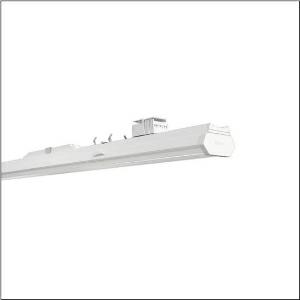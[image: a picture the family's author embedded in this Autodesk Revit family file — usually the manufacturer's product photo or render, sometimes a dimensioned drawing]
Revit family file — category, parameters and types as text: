
# Revit family: licross_r__11_protected_mo_51td12vn475f_93a6
name_source: partatom
category: Lighting Fixtures
units: mm (PartAtom-declared; Revit-internal decimal feet)

## family parameters
Cut with Voids When Loaded = No
Host = Face
Light Source = No
Part Type = Normal
Room Calculation Point = No
Round Connector Dimension = Use Diameter
Shared = No

## types (1)
- --- (1 x LED, 7910 lm, 49.3 W, 4000K)
    Apparent Load = 49 VA
    CIE Flux Codes = 73 92 98 99 100
    Color Rendering = 80
    Color Temperature = 4000K
    Default Elevation = 1800 mm
    Description = Licross® 11 Protected MO, luminaire insert, of sheet steel, galvanised, coil coated, white, length: 1.500mm, width: 90mm, height: 101mm, LED rated luminous flux: 7.910lm, light colour: 840, control gear: DALI 2, CLO, control gear: ECG DALI, with plug, 5-pole, with phase selection, mains connection: 220..240V, AC, 50/60Hz, halogen-free wiring, primary optical cover: cover, of PMMA, light emission: direct with ceiling illumination distribution, protection rating (complete): IP54, insulation class (complete): insulation class I (protective earthing), certification: CE, ENEC, VDE, UKCA, protection symbol: D if used in an environment with non-conductive dust loads with corresponding accessories, permissible ambient temperature for indoor applications: -25..+35°C, corresponds to IFS (International Featured Standards) requirements for safety and quality in the food industry, reducing of maximum allowable ambient temperature of 5°C with ceiling mounting, LABS conformity tested according to VDMA 24364:2018-05, packaging unit: 1 piece
    Height = 92 mm
    Lamp = 1 x LED
    Lamp Light Flux = 7910 lm
    Lamp Power = 49.3 W
    Lamp count = 1
    Length = 1500 mm
    Luminous efficacy = 160 lm/W
    Manufacturer = Siteco
    ModVariant = No
    Model = 51TD12VN475F
    Mounting Place = Ceiling
    Mounting Type = Pendant
    Number of Poles = 1
    OnlyDefault = Yes
    Power Factor = 1
    Product Name = Licross® 11 Protected MO
    Product group = luminaire insert
    ProductGroupID = 902
    Protection Class = Protection class I
    Protection Degree = IP 54
    RLX_Detail_Level = 1
    RlxData = <blob elided: 24433 chars, md5=553735bd>
    Socket = socket
    Standby Power = 0 W
    System Light Flux = 7910 lm
    System Power = 49 W
    Type Comments = factory setting: luminous flux: 100 % | dim-lin: 254 | 325 mA
    Type Image = l_1256145.jpg
    URL = http://relux.com
    VarID = @adj_060621
    Voltage = 0 V
    Weight = 0.00 kg
    Width = 88 mm

## geometry (parser evidence)
native form markers: Blend x4, Sweep x11
no freeform markers — native parametric forms only
